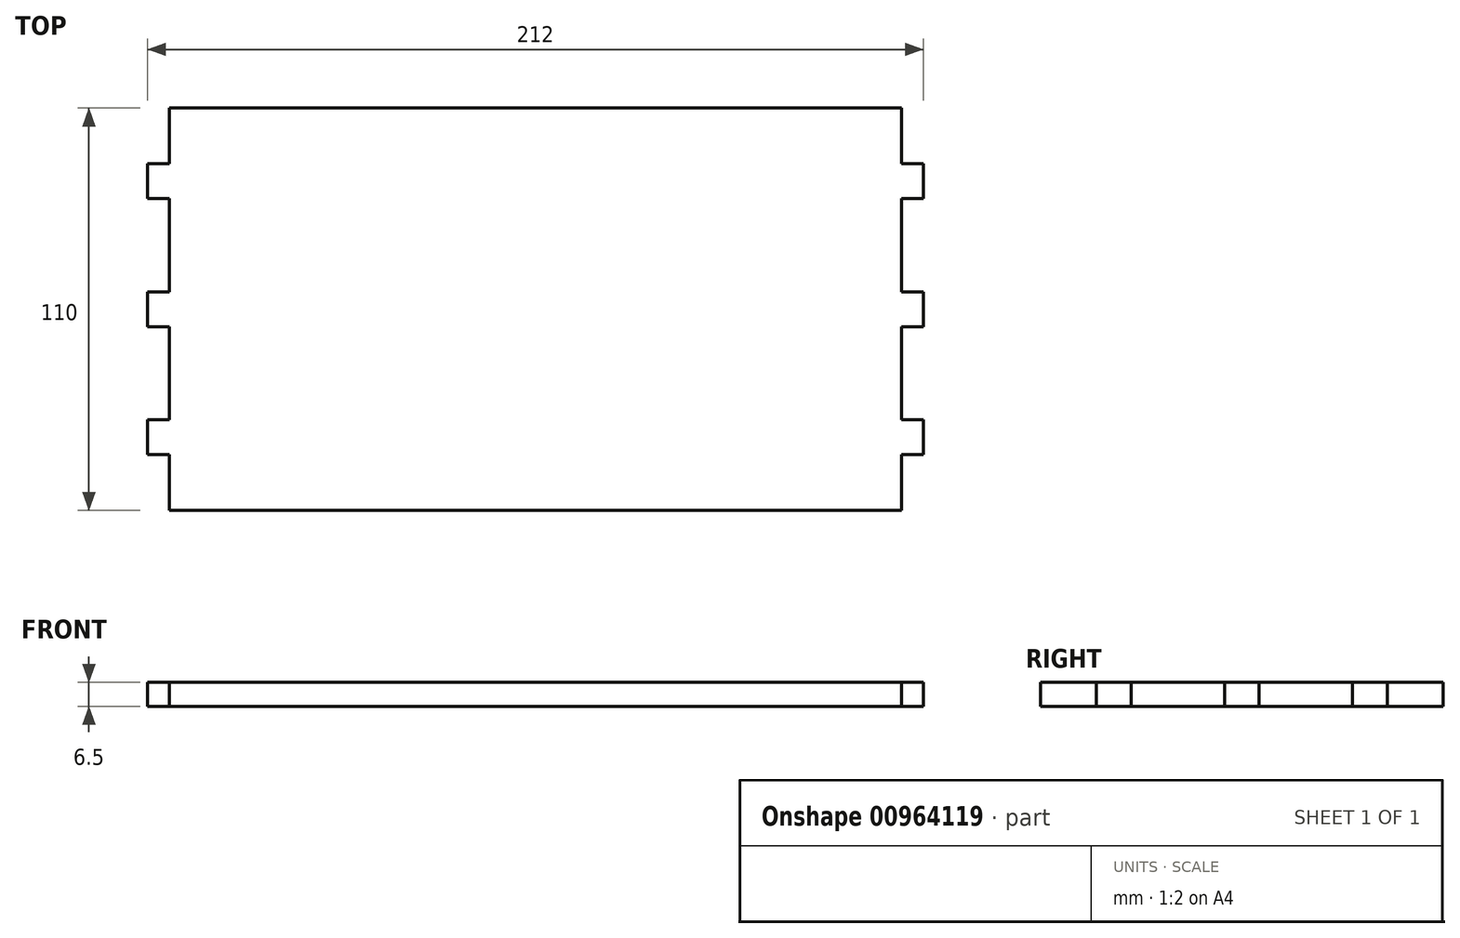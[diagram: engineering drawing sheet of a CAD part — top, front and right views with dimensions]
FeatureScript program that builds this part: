
annotation { "Feature Type Name" : "Feature", "Feature Type Description" : "" }
export const myFeature = defineFeature(function(context is Context, id is Id, definition is map)
    precondition{}
    {
        {
            var Q0;
            Q0=qCreatedBy(makeId("Top.planeOp"),FACE);
            var sketch = newSketch(context, id + "F0", { "sketchPlane" : qUnion([Q0])});
            skLineSegment(sketch, "E0.bottom", {"start": v(-100, 55) * mm, "end": v(100, 55) * mm});
            skLineSegment(sketch, "E0.top", {"start": v(-100, -55) * mm, "end": v(100, -55) * mm});
            skLineSegment(sketch, "E0.left", {"start": v(-100, 55) * mm, "end": v(-100, -55) * mm});
            skLineSegment(sketch, "E0.right", {"start": v(100, 55) * mm, "end": v(100, -55) * mm});
            skPoint(sketch, "E0.middle", {"position": v(0, 0) * mm});
            skSolve(sketch);
        }
        {
            var Q0;
            Q0=makeQuery(id+"F0.imprint","IMPRINT",FACE,{"disambiguationData":[TD([[makeQuery(id+"F0.imprint","IMPRINT",EDGE,{"derivedFrom":sQuery(id+"F0.wireOp",EDGE,"E0.bottom")}),-1.0]])]});
            extrude(context, id + "F1", {"entities" : qUnion([Q0]), "depth" : 6.5 * mm, "offsetDistance" : 25 * mm});
        }
        {
            var Q0;
            Q0=makeQuery(id+"F1.opExtrude","SWEPT_FACE",FACE,{"disambiguationData":[OSD([sQuery(id+"F0.wireOp",EDGE,"E0.left")])]});
            var sketch = newSketch(context, id + "F2", { "sketchPlane" : qUnion([Q0])});
            skLineSegment(sketch, "E1", {"start": v(-55, 3.25) * mm, "end": v(-35, 3.25) * mm});
            skLineSegment(sketch, "E2", {"start": v(-35, 3.25) * mm, "end": v(0, 3.25) * mm});
            skLineSegment(sketch, "E3", {"start": v(0, 3.25) * mm, "end": v(35, 3.25) * mm});
            skLineSegment(sketch, "E4", {"start": v(35, 3.25) * mm, "end": v(55, 3.25) * mm});
            skLineSegment(sketch, "E5.bottom", {"start": v(-39.75, 6.5) * mm, "end": v(-30.25, 6.5) * mm});
            skLineSegment(sketch, "E5.top", {"start": v(-39.75, 0) * mm, "end": v(-30.25, 0) * mm});
            skLineSegment(sketch, "E5.left", {"start": v(-39.75, 6.5) * mm, "end": v(-39.75, 0) * mm});
            skLineSegment(sketch, "E5.right", {"start": v(-30.25, 6.5) * mm, "end": v(-30.25, 0) * mm});
            skPoint(sketch, "E5.middle", {"position": v(-35, 3.25) * mm});
            skLineSegment(sketch, "E6.bottom", {"start": v(-4.75, 6.5) * mm, "end": v(4.75, 6.5) * mm});
            skLineSegment(sketch, "E6.top", {"start": v(-4.75, 0) * mm, "end": v(4.75, 0) * mm});
            skLineSegment(sketch, "E6.left", {"start": v(-4.75, 6.5) * mm, "end": v(-4.75, 0) * mm});
            skLineSegment(sketch, "E6.right", {"start": v(4.75, 6.5) * mm, "end": v(4.75, 0) * mm});
            skPoint(sketch, "E6.middle", {"position": v(0, 3.25) * mm});
            skLineSegment(sketch, "E7.bottom", {"start": v(39.75, 6.5) * mm, "end": v(30.25, 6.5) * mm});
            skLineSegment(sketch, "E7.top", {"start": v(39.75, 0) * mm, "end": v(30.25, 0) * mm});
            skLineSegment(sketch, "E7.left", {"start": v(39.75, 6.5) * mm, "end": v(39.75, 0) * mm});
            skLineSegment(sketch, "E7.right", {"start": v(30.25, 6.5) * mm, "end": v(30.25, 0) * mm});
            skPoint(sketch, "E7.middle", {"position": v(35, 3.25) * mm});
            skSolve(sketch);
        }
        {
            var Q0;
            {var subQ0=sQuery(id+"F2.wireOp",EDGE,"E5.bottom");Q0=makeQuery(id+"F2.imprint","IMPRINT",FACE,{"disambiguationData":[TD([[makeQuery(id+"F2.imprint","IMPRINT",EDGE,{"derivedFrom":subQ0}),-1.0]])]});}
            var Q1;
            {var subQ1=sQuery(id+"F2.wireOp",EDGE,"E5.top");Q1=makeQuery(id+"F2.imprint","IMPRINT",FACE,{"disambiguationData":[TD([[makeQuery(id+"F2.imprint","IMPRINT",EDGE,{"derivedFrom":subQ1}),1.0]])]});}
            var Q2;
            {var subQ1=sQuery(id+"F2.wireOp",EDGE,"E6.bottom");Q2=makeQuery(id+"F2.imprint","IMPRINT",FACE,{"disambiguationData":[TD([[makeQuery(id+"F2.imprint","IMPRINT",EDGE,{"derivedFrom":subQ1}),-1.0]])]});}
            var Q3;
            {var subQ0=sQuery(id+"F2.wireOp",EDGE,"E6.top");Q3=makeQuery(id+"F2.imprint","IMPRINT",FACE,{"disambiguationData":[TD([[makeQuery(id+"F2.imprint","IMPRINT",EDGE,{"derivedFrom":subQ0}),1.0]])]});}
            var Q4;
            {var subQ1=sQuery(id+"F2.wireOp",EDGE,"E7.bottom");Q4=makeQuery(id+"F2.imprint","IMPRINT",FACE,{"disambiguationData":[TD([[makeQuery(id+"F2.imprint","IMPRINT",EDGE,{"derivedFrom":subQ1}),-1.0]])]});}
            var Q5;
            {var subQ1=sQuery(id+"F2.wireOp",EDGE,"E7.top");Q5=makeQuery(id+"F2.imprint","IMPRINT",FACE,{"disambiguationData":[TD([[makeQuery(id+"F2.imprint","IMPRINT",EDGE,{"derivedFrom":subQ1}),1.0]])]});}
            extrude(context, id + "F3", {"entities" : qUnion([Q0, Q1, Q2, Q3, Q4, Q5]), "operationType" : NewBodyOperationType.ADD, "depth" : 6 * mm, "offsetDistance" : 25 * mm});
        }
        {
            var Q0;
            Q0=makeQuery(id+"F1.opExtrude","SWEPT_FACE",FACE,{"disambiguationData":[OSD([sQuery(id+"F0.wireOp",EDGE,"E0.right")])]});
            var sketch = newSketch(context, id + "F4", { "sketchPlane" : qUnion([Q0])});
            skLineSegment(sketch, "E8", {"start": v(-55, 3.25) * mm, "end": v(-35, 3.25) * mm});
            skLineSegment(sketch, "E9", {"start": v(-35, 3.25) * mm, "end": v(0, 3.25) * mm});
            skLineSegment(sketch, "E10", {"start": v(0, 3.25) * mm, "end": v(35, 3.25) * mm});
            skLineSegment(sketch, "E11.bottom", {"start": v(-39.75, 6.5) * mm, "end": v(-30.25, 6.5) * mm});
            skLineSegment(sketch, "E11.top", {"start": v(-39.75, 0) * mm, "end": v(-30.25, 0) * mm});
            skLineSegment(sketch, "E11.left", {"start": v(-39.75, 6.5) * mm, "end": v(-39.75, 0) * mm});
            skLineSegment(sketch, "E11.right", {"start": v(-30.25, 6.5) * mm, "end": v(-30.25, 0) * mm});
            skPoint(sketch, "E11.middle", {"position": v(-35, 3.25) * mm});
            skLineSegment(sketch, "E12.bottom", {"start": v(-4.75, 6.5) * mm, "end": v(4.75, 6.5) * mm});
            skLineSegment(sketch, "E12.top", {"start": v(-4.75, 0) * mm, "end": v(4.75, 0) * mm});
            skLineSegment(sketch, "E12.left", {"start": v(-4.75, 6.5) * mm, "end": v(-4.75, 0) * mm});
            skLineSegment(sketch, "E12.right", {"start": v(4.75, 6.5) * mm, "end": v(4.75, 0) * mm});
            skPoint(sketch, "E12.middle", {"position": v(0, 3.25) * mm});
            skLineSegment(sketch, "E13.bottom", {"start": v(39.75, 6.5) * mm, "end": v(30.25, 6.5) * mm});
            skLineSegment(sketch, "E13.top", {"start": v(39.75, 0) * mm, "end": v(30.25, 0) * mm});
            skLineSegment(sketch, "E13.left", {"start": v(39.75, 6.5) * mm, "end": v(39.75, 0) * mm});
            skLineSegment(sketch, "E13.right", {"start": v(30.25, 6.5) * mm, "end": v(30.25, 0) * mm});
            skPoint(sketch, "E13.middle", {"position": v(35, 3.25) * mm});
            skSolve(sketch);
        }
        {
            var Q0;
            {var subQ1=sQuery(id+"F4.wireOp",EDGE,"E11.bottom");Q0=makeQuery(id+"F4.imprint","IMPRINT",FACE,{"disambiguationData":[TD([[makeQuery(id+"F4.imprint","IMPRINT",EDGE,{"derivedFrom":subQ1}),1.0]])]});}
            var Q1;
            {var subQ1=sQuery(id+"F4.wireOp",EDGE,"E11.top");Q1=makeQuery(id+"F4.imprint","IMPRINT",FACE,{"disambiguationData":[TD([[makeQuery(id+"F4.imprint","IMPRINT",EDGE,{"derivedFrom":subQ1}),-1.0]])]});}
            var Q2;
            {var subQ0=sQuery(id+"F4.wireOp",EDGE,"E12.bottom");Q2=makeQuery(id+"F4.imprint","IMPRINT",FACE,{"disambiguationData":[TD([[makeQuery(id+"F4.imprint","IMPRINT",EDGE,{"derivedFrom":subQ0}),1.0]])]});}
            var Q3;
            {var subQ1=sQuery(id+"F4.wireOp",EDGE,"E12.top");Q3=makeQuery(id+"F4.imprint","IMPRINT",FACE,{"disambiguationData":[TD([[makeQuery(id+"F4.imprint","IMPRINT",EDGE,{"derivedFrom":subQ1}),-1.0]])]});}
            var Q4;
            {var subQ1=sQuery(id+"F4.wireOp",EDGE,"E13.bottom");Q4=makeQuery(id+"F4.imprint","IMPRINT",FACE,{"disambiguationData":[TD([[makeQuery(id+"F4.imprint","IMPRINT",EDGE,{"derivedFrom":subQ1}),1.0]])]});}
            extrude(context, id + "F5", {"entities" : qUnion([Q0, Q1, Q2, Q3, Q4]), "operationType" : NewBodyOperationType.ADD, "depth" : 6 * mm, "offsetDistance" : 25 * mm});
        }
    });
